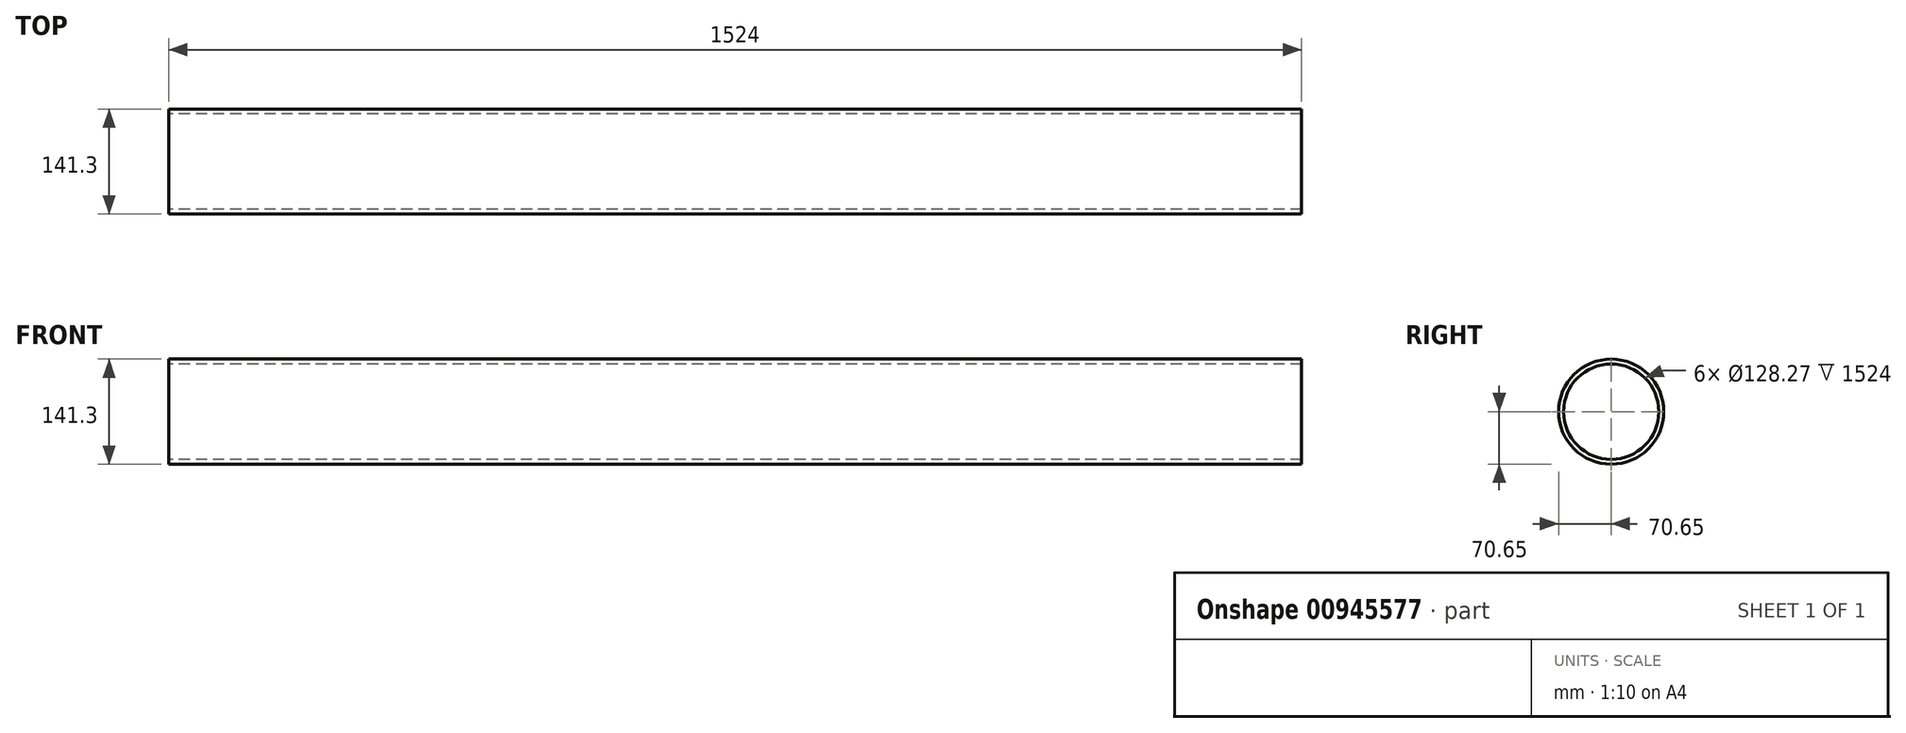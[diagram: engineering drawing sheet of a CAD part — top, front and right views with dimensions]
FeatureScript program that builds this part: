
annotation { "Feature Type Name" : "Feature", "Feature Type Description" : "" }
export const myFeature = defineFeature(function(context is Context, id is Id, definition is map)
    precondition{}
    {
        {
            var Q0;
            Q0=qCreatedBy(makeId("Right.planeOp"),FACE);
            var sketch = newSketch(context, id + "F0", { "sketchPlane" : qUnion([Q0])});
            skCircle(sketch, "E0", {"center": v(0, 0) * mm, "radius": 70.65 * mm});
            skCircle(sketch, "E1", {"center": v(0, 0) * mm, "radius": 64.13 * mm});
            skSolve(sketch);
        }
        {
            var Q0;
            Q0=makeQuery(id+"F0.imprint","IMPRINT",FACE,{"disambiguationData":[TD([[makeQuery(id+"F0.imprint","IMPRINT",EDGE,{"derivedFrom":sQuery(id+"F0.wireOp",EDGE,"E0")}),1.0]])]});
            extrude(context, id + "F1", {"entities" : qUnion([Q0]), "depth" : 1524 * mm, "offsetDistance" : 25.4 * mm});
        }
    });
